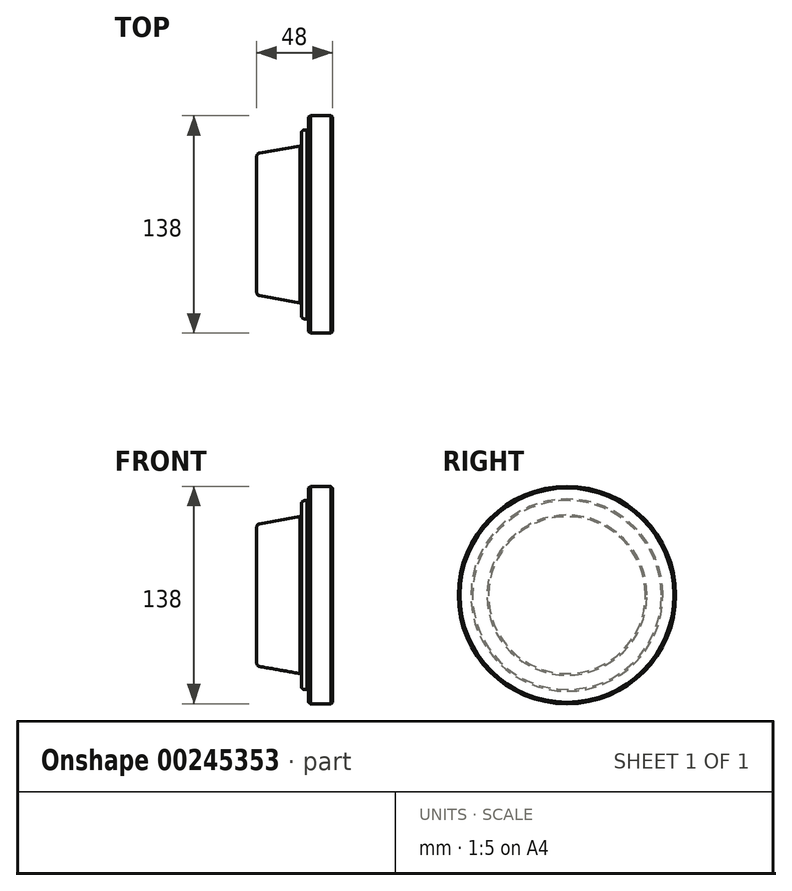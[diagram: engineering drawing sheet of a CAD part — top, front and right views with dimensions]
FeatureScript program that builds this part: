
annotation { "Feature Type Name" : "Feature", "Feature Type Description" : "" }
export const myFeature = defineFeature(function(context is Context, id is Id, definition is map)
    precondition{}
    {
        {
            var Q0;
            Q0=qCreatedBy(makeId("Front.planeOp"),FACE);
            var sketch = newSketch(context, id + "F0", { "sketchPlane" : qUnion([Q0])});
            skLineSegment(sketch, "E0", {"start": v(0, 0) * mm, "end": v(0, 43.32) * mm});
            skLineSegment(sketch, "E1", {"start": v(1.65, 45.3) * mm, "end": v(28.36, 50) * mm});
            skLineSegment(sketch, "E2", {"start": v(28.36, 50) * mm, "end": v(28.36, 58) * mm});
            skLineSegment(sketch, "E3", {"start": v(30.36, 60) * mm, "end": v(33, 60) * mm});
            skLineSegment(sketch, "E4", {"start": v(33, 60) * mm, "end": v(33, 69) * mm});
            skLineSegment(sketch, "E5", {"start": v(33, 69) * mm, "end": v(48, 69) * mm});
            skLineSegment(sketch, "E6", {"start": v(48, 69) * mm, "end": v(48, 0) * mm});
            skLineSegment(sketch, "E7", {"start": v(48, 0) * mm, "end": v(0, 0) * mm});
            skPoint(sketch, "E8.visualSharp", {"position": v(28.36, 60) * mm});
            skArc(sketch, "E8.filletArc", {"start": v(30.36, 60) * mm, "mid": v(28.94, 59.41) * mm, "end": v(28.36, 58) * mm});
            skPoint(sketch, "E9.visualSharp", {"position": v(0, 45) * mm});
            skArc(sketch, "E9.filletArc", {"start": v(1.65, 45.3) * mm, "mid": v(0.47, 44.6) * mm, "end": v(0, 43.32) * mm});
            skSolve(sketch);
        }
        {
            var Q0;
            Q0=makeQuery(id+"F0.imprint","IMPRINT",FACE,{"disambiguationData":[TD([[makeQuery(id+"F0.imprint","IMPRINT",EDGE,{"derivedFrom":sQuery(id+"F0.wireOp",EDGE,"E0")}),-1.0]])]});
            var Q1;
            Q1=sQuery(id+"F0.wireOp",EDGE,"E7");
            revolve(context, id + "F1", {"entities" : qUnion([Q0]), "axis" : qUnion([Q1]), "revolveType" : RevolveType.FULL});
        }
        {
            var Q0;
            Q0=makeQuery(id+"F1.opRevolve","SWEPT_EDGE",EDGE,{"disambiguationData":[OSD([sQuery(id+"F0.wireOp",EDGE,"E5"),sQuery(id+"F0.wireOp",EDGE,"E6")])]});
            var Q1;
            Q1=makeQuery(id+"F1.opRevolve","SWEPT_EDGE",EDGE,{"disambiguationData":[OSD([sQuery(id+"F0.wireOp",EDGE,"E4"),sQuery(id+"F0.wireOp",EDGE,"E5")])]});
            var Q2;
            Q2=makeQuery(id+"F1.opRevolve","SWEPT_FACE",FACE,{"disambiguationData":[OSD([sQuery(id+"F0.wireOp",EDGE,"E1")])]});
            var Q3;
            Q3=makeQuery(id+"F1.opRevolve","SWEPT_EDGE",EDGE,{"disambiguationData":[OSD([sQuery(id+"F0.wireOp",EDGE,"E2"),sQuery(id+"F0.wireOp",EDGE,"E3")])]});
            chamfer(context, id + "F2", {"entities" : qUnion([Q0, Q1, Q2, Q3]), "width" : 1 * mm, "tangentPropagation" : true});
        }
    });
